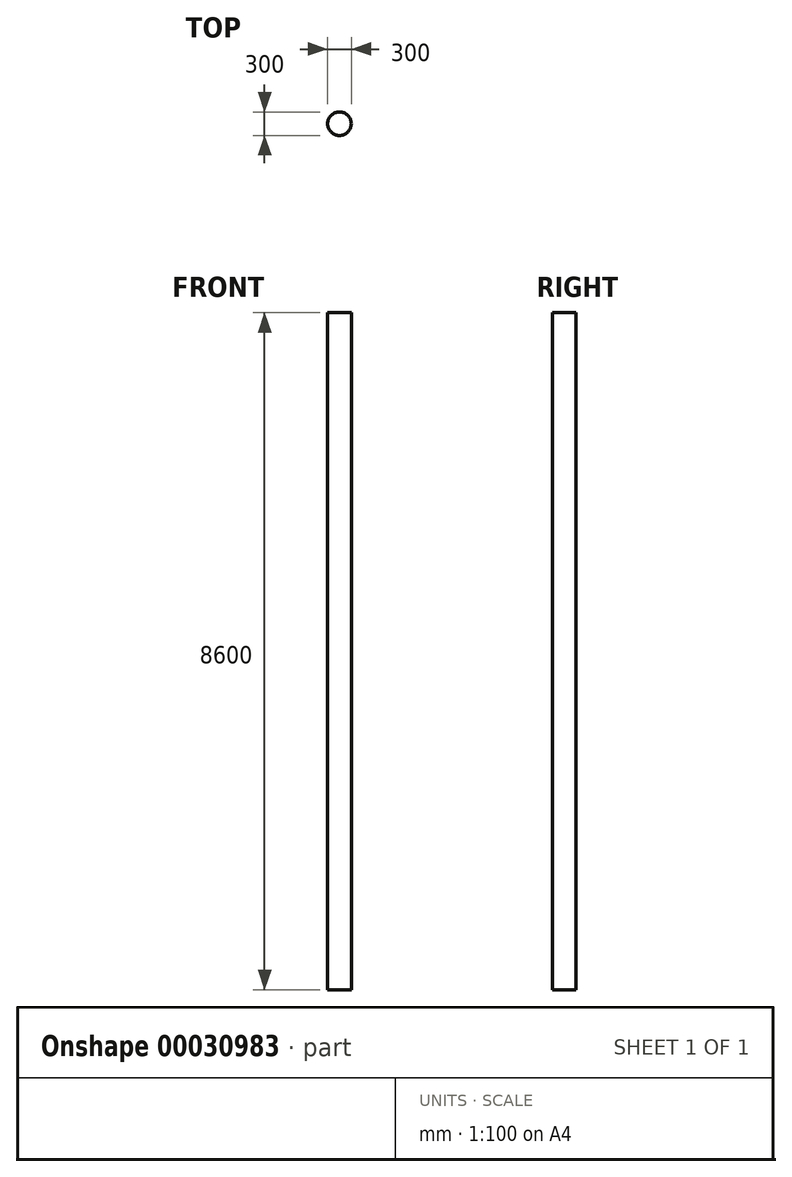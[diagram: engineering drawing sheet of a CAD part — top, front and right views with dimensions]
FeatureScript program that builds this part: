
annotation { "Feature Type Name" : "Feature", "Feature Type Description" : "" }
export const myFeature = defineFeature(function(context is Context, id is Id, definition is map)
    precondition{}
    {
        {
            var Q0;
            Q0=qCreatedBy(makeId("Top.planeOp"),FACE);
            var sketch = newSketch(context, id + "F0", { "sketchPlane" : qUnion([Q0])});
            skCircle(sketch, "E0", {"center": v(0, 0) * mm, "radius": 150 * mm});
            skSolve(sketch);
        }
        {
            var Q0;
            Q0 = qSketchRegion(id + "F0", true);
            extrude(context, id + "F1", {"entities" : qUnion([Q0]), "depth" : 8600 * mm});
        }
    });
